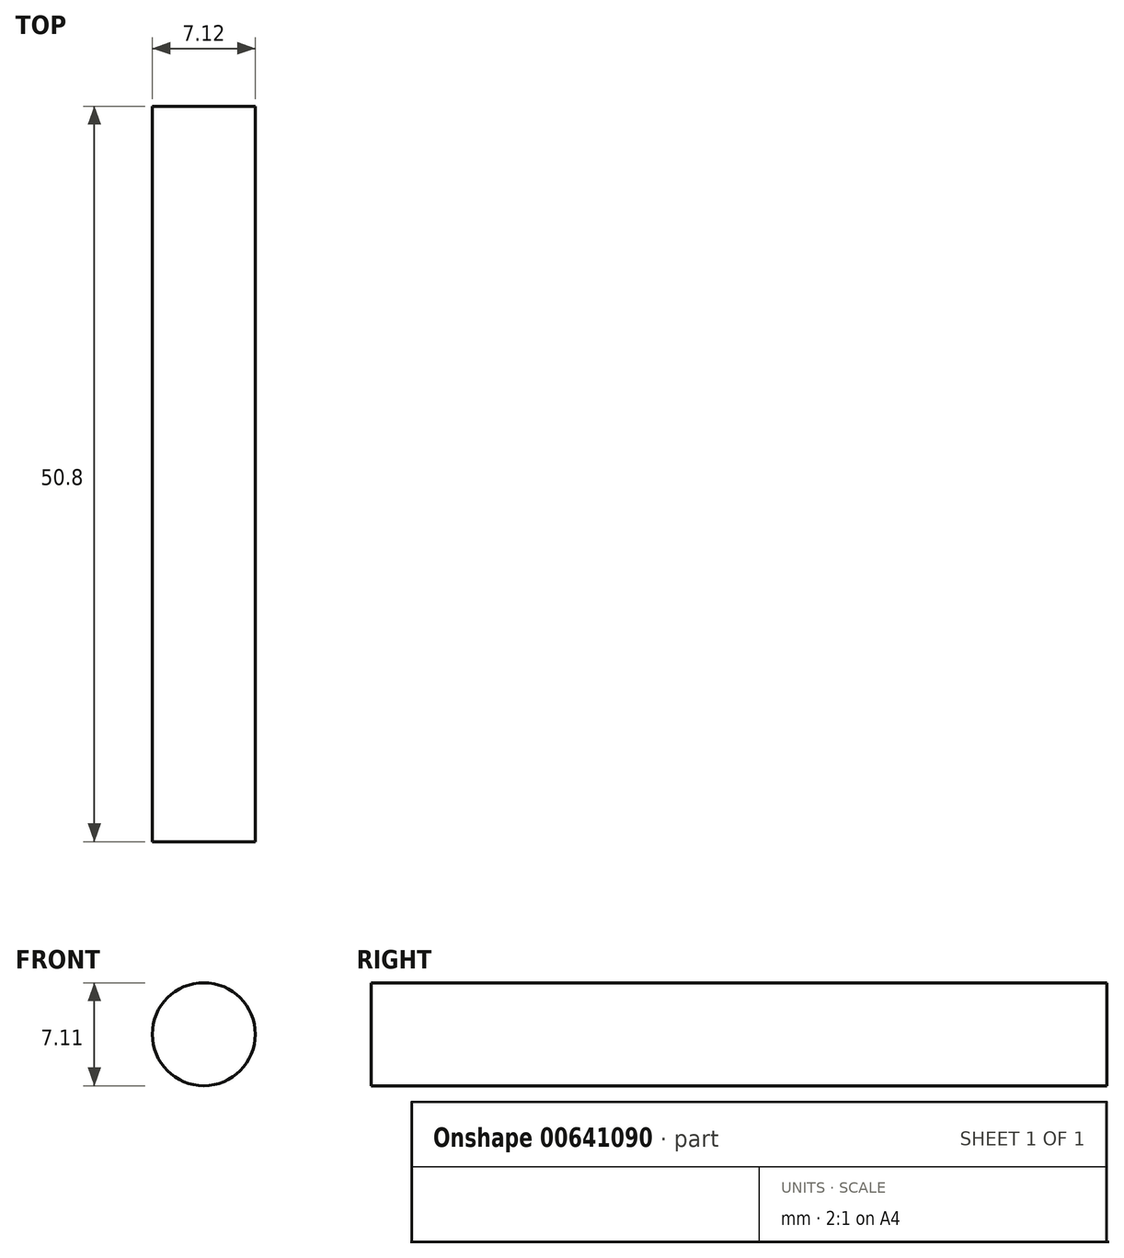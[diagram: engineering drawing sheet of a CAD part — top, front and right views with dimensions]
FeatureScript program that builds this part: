
annotation { "Feature Type Name" : "Feature", "Feature Type Description" : "" }
export const myFeature = defineFeature(function(context is Context, id is Id, definition is map)
    precondition{}
    {
        {
            var Q0;
            Q0=qCreatedBy(makeId("Front.planeOp"),FACE);
            var sketch = newSketch(context, id + "F0", { "sketchPlane" : qUnion([Q0])});
            skCircle(sketch, "E0", {"center": v(-46.62, 32.36) * mm, "radius": 3.56 * mm});
            skSolve(sketch);
        }
        {
            var Q0;
            Q0 = qSketchRegion(id + "F0", true);
            extrude(context, id + "F1", {"entities" : qUnion([Q0]), "depth" : 50.8 * mm, "offsetDistance" : 25.4 * mm});
        }
    });
